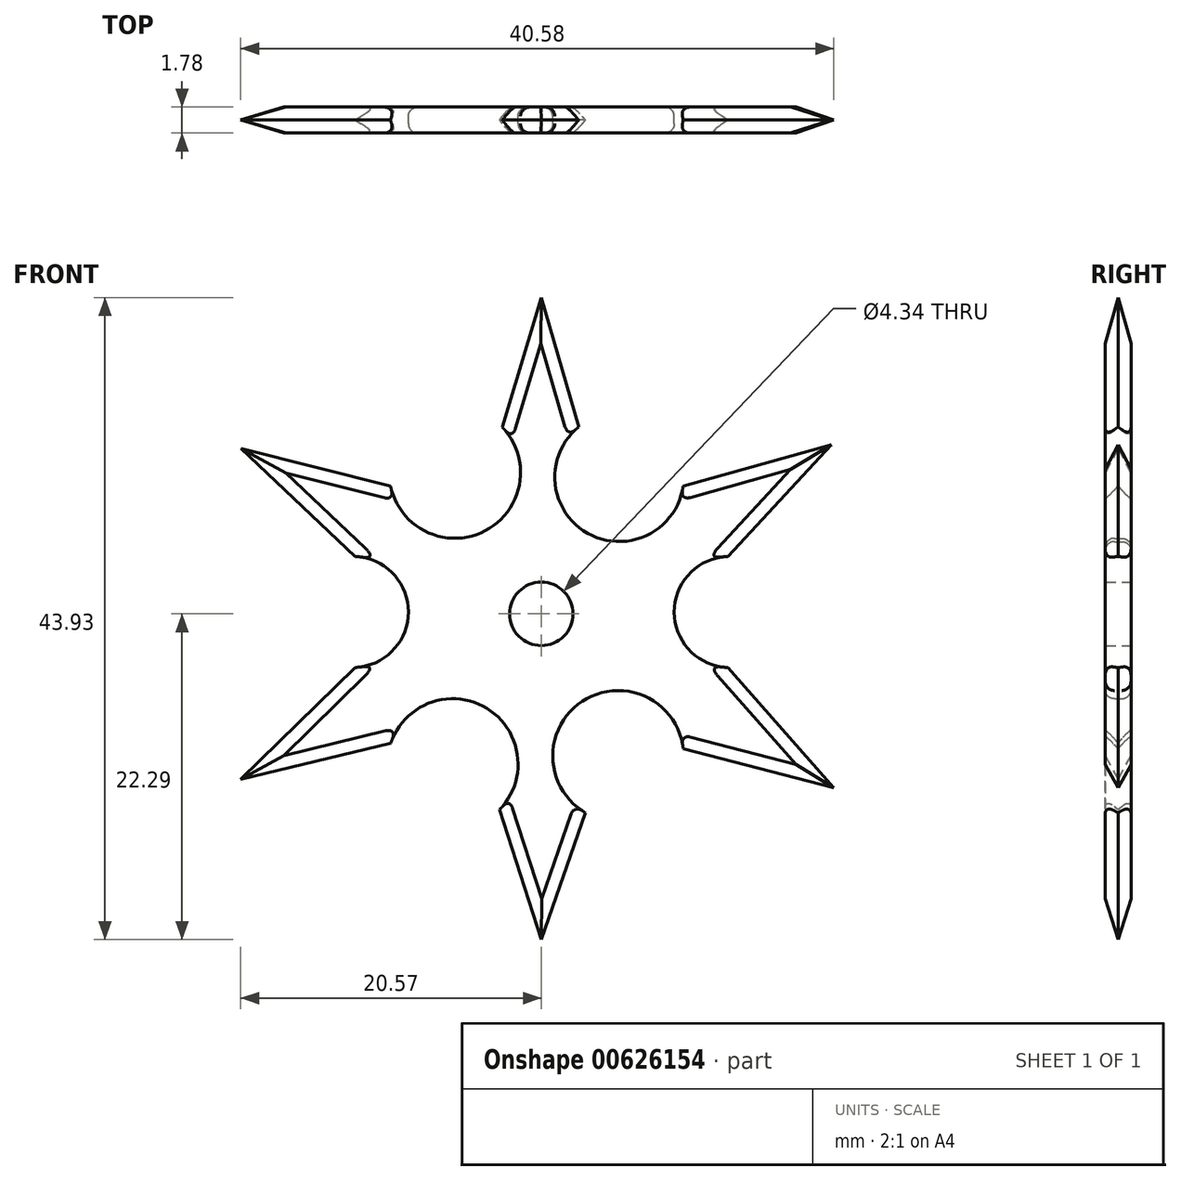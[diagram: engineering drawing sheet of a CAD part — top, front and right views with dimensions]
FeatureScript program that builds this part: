
annotation { "Feature Type Name" : "Feature", "Feature Type Description" : "" }
export const myFeature = defineFeature(function(context is Context, id is Id, definition is map)
    precondition{}
    {
        {
            var Q0;
            Q0=qCreatedBy(makeId("Front.planeOp"),FACE);
            var sketch = newSketch(context, id + "F0", { "sketchPlane" : qUnion([Q0])});
            skCircle(sketch, "E0", {"center": v(0, 0) * mm, "radius": 4.02 * mm});
            skArc(sketch, "E1", {"start": v(-12.92, -3.67) * mm, "mid": v(-9.1, 0.13) * mm, "end": v(-12.92, 3.93) * mm});
            skArc(sketch, "E2", {"start": v(12.92, 3.93) * mm, "mid": v(9.1, 0.13) * mm, "end": v(12.92, -3.67) * mm});
            skPoint(sketch, "E3.startSnap0", {"position": v(-9.1, 0.13) * mm});
            skLineSegment(sketch, "E4", {"start": v(-12.92, -3.67) * mm, "end": v(-20.98, -11.56) * mm});
            skLineSegment(sketch, "E5", {"start": v(-20.98, -11.56) * mm, "end": v(-10.34, -8.98) * mm});
            skLineSegment(sketch, "E6", {"start": v(9.72, -9.35) * mm, "end": v(20.38, -12.12) * mm});
            skLineSegment(sketch, "E7", {"start": v(12.92, -3.67) * mm, "end": v(20.38, -12.12) * mm});
            skLineSegment(sketch, "E8", {"start": v(12.92, 3.93) * mm, "end": v(20.25, 11.82) * mm});
            skLineSegment(sketch, "E9", {"start": v(9.72, 8.88) * mm, "end": v(20.25, 11.82) * mm});
            skLineSegment(sketch, "E10", {"start": v(-12.92, 3.93) * mm, "end": v(-20.98, 11.55) * mm});
            skLineSegment(sketch, "E11", {"start": v(-10.34, 8.88) * mm, "end": v(-20.98, 11.55) * mm});
            skCircle(sketch, "E12", {"center": v(0, 0) * mm, "radius": 2.17 * mm});
            skArc(sketch, "E13", {"start": v(-2.96, -13.5) * mm, "mid": v(-3.73, -6.46) * mm, "end": v(-10.34, -8.98) * mm});
            skArc(sketch, "E14", {"start": v(9.72, -9.35) * mm, "mid": v(2.8, -5.98) * mm, "end": v(3.13, -13.66) * mm});
            skLineSegment(sketch, "E15", {"start": v(-2.96, -13.5) * mm, "end": v(0, -22.69) * mm});
            skLineSegment(sketch, "E16", {"start": v(0, -22.69) * mm, "end": v(3.13, -13.66) * mm});
            skArc(sketch, "E17", {"start": v(-10.34, 8.88) * mm, "mid": v(-3.82, 5.69) * mm, "end": v(-2.77, 12.87) * mm});
            skArc(sketch, "E18", {"start": v(2.66, 12.87) * mm, "mid": v(3.16, 5.52) * mm, "end": v(9.72, 8.88) * mm});
            skLineSegment(sketch, "E19", {"start": v(-2.77, 12.87) * mm, "end": v(0, 22.1) * mm});
            skLineSegment(sketch, "E20", {"start": v(0, 22.1) * mm, "end": v(2.66, 12.87) * mm});
            skLineSegment(sketch, "E21", {"start": v(-2.77, 12.87) * mm, "end": v(2.66, 12.87) * mm});
            skLineSegment(sketch, "E22", {"start": v(-2.96, -13.5) * mm, "end": v(3.13, -13.66) * mm});
            skLineSegment(sketch, "E23", {"start": v(-12.92, -3.67) * mm, "end": v(-10.34, -8.98) * mm});
            skLineSegment(sketch, "E24", {"start": v(-12.92, 3.93) * mm, "end": v(-10.34, 8.88) * mm});
            skLineSegment(sketch, "E25", {"start": v(9.72, 8.88) * mm, "end": v(12.92, 3.93) * mm});
            skLineSegment(sketch, "E26", {"start": v(12.92, -3.67) * mm, "end": v(9.72, -9.35) * mm});
            skPoint(sketch, "E27.endSnap0", {"position": v(-11.63, 6.4) * mm});
            skLineSegment(sketch, "E28", {"start": v(-11.63, 6.4) * mm, "end": v(-20.98, 11.55) * mm});
            skLineSegment(sketch, "E29", {"start": v(0, 22.1) * mm, "end": v(0, 12.87) * mm});
            skLineSegment(sketch, "E30", {"start": v(20.25, 11.82) * mm, "end": v(11.32, 6.4) * mm});
            skLineSegment(sketch, "E31", {"start": v(20.38, -12.12) * mm, "end": v(11.32, -6.51) * mm});
            skLineSegment(sketch, "E32", {"start": v(0, -22.69) * mm, "end": v(0, -13.58) * mm});
            skLineSegment(sketch, "E33", {"start": v(-20.98, -11.56) * mm, "end": v(-11.63, -6.32) * mm});
            skLineSegment(sketch, "E34", {"start": v(-12.92, 3.93) * mm, "end": v(-16.3, 8.98) * mm});
            skLineSegment(sketch, "E35", {"start": v(-16.3, 8.98) * mm, "end": v(-10.34, 8.88) * mm});
            skLineSegment(sketch, "E36", {"start": v(-10.34, -8.98) * mm, "end": v(-16.38, -8.98) * mm});
            skLineSegment(sketch, "E37", {"start": v(-16.38, -8.98) * mm, "end": v(-12.92, -3.67) * mm});
            skLineSegment(sketch, "E38", {"start": v(-2.96, -13.5) * mm, "end": v(0, -18.8) * mm});
            skLineSegment(sketch, "E39", {"start": v(0, -18.8) * mm, "end": v(3.13, -13.66) * mm});
            skLineSegment(sketch, "E40", {"start": v(9.72, -9.35) * mm, "end": v(16.19, -9.53) * mm});
            skLineSegment(sketch, "E41", {"start": v(16.19, -9.53) * mm, "end": v(12.92, -3.67) * mm});
            skLineSegment(sketch, "E42", {"start": v(-2.77, 12.87) * mm, "end": v(0, 17.48) * mm});
            skLineSegment(sketch, "E43", {"start": v(0, 17.48) * mm, "end": v(2.66, 12.87) * mm});
            skPoint(sketch, "E44.endSnap0", {"position": v(15.78, 9.11) * mm});
            skLineSegment(sketch, "E45", {"start": v(9.72, 8.88) * mm, "end": v(15.78, 9.11) * mm});
            skLineSegment(sketch, "E46", {"start": v(15.78, 9.11) * mm, "end": v(12.92, 3.93) * mm});
            skSolve(sketch);
        }
        {
            var Q0;
            Q0=makeQuery(id+"F0.imprint","IMPRINT",FACE,{"disambiguationData":[TD([[makeQuery(id+"F0.imprint","IMPRINT",EDGE,{"derivedFrom":sQuery(id+"F0.wireOp",EDGE,"E0")}),-1.0]])]});
            var Q1;
            Q1=makeQuery(id+"F0.imprint","IMPRINT",FACE,{"disambiguationData":[TD([[makeQuery(id+"F0.imprint","IMPRINT",EDGE,{"derivedFrom":sQuery(id+"F0.wireOp",EDGE,"E0")}),1.0]])]});
            extrude(context, id + "F1", {"entities" : qUnion([Q0, Q1]), "depth" : 1.78 * mm, "symmetric" : true});
        }
        {
            var Q0;
            {var subQ0=sQuery(id+"F0.wireOp",EDGE,"E35");Q0=makeQuery(id+"F0.imprint","IMPRINT",FACE,{"disambiguationData":[TD([[makeQuery(id+"F0.imprint","IMPRINT",EDGE,{"derivedFrom":subQ0}),-1.0]])]});}
            var Q1;
            {var subQ0=sQuery(id+"F0.wireOp",EDGE,"E34");Q1=makeQuery(id+"F0.imprint","IMPRINT",FACE,{"disambiguationData":[TD([[makeQuery(id+"F0.imprint","IMPRINT",EDGE,{"derivedFrom":subQ0}),-1.0]])]});}
            var Q2;
            {var subQ0=sQuery(id+"F0.wireOp",EDGE,"E10");Q2=makeQuery(id+"F0.imprint","IMPRINT",FACE,{"disambiguationData":[TD([[makeQuery(id+"F0.imprint","IMPRINT",EDGE,{"derivedFrom":subQ0}),-1.0]])]});}
            var Q3;
            {var subQ0=sQuery(id+"F0.wireOp",EDGE,"E11");Q3=makeQuery(id+"F0.imprint","IMPRINT",FACE,{"disambiguationData":[TD([[makeQuery(id+"F0.imprint","IMPRINT",EDGE,{"derivedFrom":subQ0}),1.0]])]});}
            var Q4;
            {var subQ0=sQuery(id+"F0.wireOp",EDGE,"E42");Q4=makeQuery(id+"F0.imprint","IMPRINT",FACE,{"disambiguationData":[TD([[makeQuery(id+"F0.imprint","IMPRINT",EDGE,{"derivedFrom":subQ0}),-1.0]])]});}
            var Q5;
            {var subQ0=sQuery(id+"F0.wireOp",EDGE,"E43");Q5=makeQuery(id+"F0.imprint","IMPRINT",FACE,{"disambiguationData":[TD([[makeQuery(id+"F0.imprint","IMPRINT",EDGE,{"derivedFrom":subQ0}),-1.0]])]});}
            var Q6;
            {var subQ0=sQuery(id+"F0.wireOp",EDGE,"E20");Q6=makeQuery(id+"F0.imprint","IMPRINT",FACE,{"disambiguationData":[TD([[makeQuery(id+"F0.imprint","IMPRINT",EDGE,{"derivedFrom":subQ0}),-1.0]])]});}
            var Q7;
            {var subQ0=sQuery(id+"F0.wireOp",EDGE,"E19");Q7=makeQuery(id+"F0.imprint","IMPRINT",FACE,{"disambiguationData":[TD([[makeQuery(id+"F0.imprint","IMPRINT",EDGE,{"derivedFrom":subQ0}),-1.0]])]});}
            var Q8;
            {var subQ0=sQuery(id+"F0.wireOp",EDGE,"E5");Q8=makeQuery(id+"F0.imprint","IMPRINT",FACE,{"disambiguationData":[TD([[makeQuery(id+"F0.imprint","IMPRINT",EDGE,{"derivedFrom":subQ0}),1.0]])]});}
            var Q9;
            {var subQ0=sQuery(id+"F0.wireOp",EDGE,"E4");Q9=makeQuery(id+"F0.imprint","IMPRINT",FACE,{"disambiguationData":[TD([[makeQuery(id+"F0.imprint","IMPRINT",EDGE,{"derivedFrom":subQ0}),1.0]])]});}
            var Q10;
            {var subQ0=sQuery(id+"F0.wireOp",EDGE,"E37");Q10=makeQuery(id+"F0.imprint","IMPRINT",FACE,{"disambiguationData":[TD([[makeQuery(id+"F0.imprint","IMPRINT",EDGE,{"derivedFrom":subQ0}),-1.0]])]});}
            var Q11;
            {var subQ0=sQuery(id+"F0.wireOp",EDGE,"E36");Q11=makeQuery(id+"F0.imprint","IMPRINT",FACE,{"disambiguationData":[TD([[makeQuery(id+"F0.imprint","IMPRINT",EDGE,{"derivedFrom":subQ0}),-1.0]])]});}
            var Q12;
            {var subQ0=sQuery(id+"F0.wireOp",EDGE,"E15");Q12=makeQuery(id+"F0.imprint","IMPRINT",FACE,{"disambiguationData":[TD([[makeQuery(id+"F0.imprint","IMPRINT",EDGE,{"derivedFrom":subQ0}),1.0]])]});}
            var Q13;
            {var subQ0=sQuery(id+"F0.wireOp",EDGE,"E16");Q13=makeQuery(id+"F0.imprint","IMPRINT",FACE,{"disambiguationData":[TD([[makeQuery(id+"F0.imprint","IMPRINT",EDGE,{"derivedFrom":subQ0}),1.0]])]});}
            var Q14;
            {var subQ0=sQuery(id+"F0.wireOp",EDGE,"E39");Q14=makeQuery(id+"F0.imprint","IMPRINT",FACE,{"disambiguationData":[TD([[makeQuery(id+"F0.imprint","IMPRINT",EDGE,{"derivedFrom":subQ0}),1.0]])]});}
            var Q15;
            {var subQ0=sQuery(id+"F0.wireOp",EDGE,"E38");Q15=makeQuery(id+"F0.imprint","IMPRINT",FACE,{"disambiguationData":[TD([[makeQuery(id+"F0.imprint","IMPRINT",EDGE,{"derivedFrom":subQ0}),1.0]])]});}
            var Q16;
            {var subQ0=sQuery(id+"F0.wireOp",EDGE,"E7");Q16=makeQuery(id+"F0.imprint","IMPRINT",FACE,{"disambiguationData":[TD([[makeQuery(id+"F0.imprint","IMPRINT",EDGE,{"derivedFrom":subQ0}),-1.0]])]});}
            var Q17;
            {var subQ0=sQuery(id+"F0.wireOp",EDGE,"E41");Q17=makeQuery(id+"F0.imprint","IMPRINT",FACE,{"disambiguationData":[TD([[makeQuery(id+"F0.imprint","IMPRINT",EDGE,{"derivedFrom":subQ0}),1.0]])]});}
            var Q18;
            {var subQ0=sQuery(id+"F0.wireOp",EDGE,"E40");Q18=makeQuery(id+"F0.imprint","IMPRINT",FACE,{"disambiguationData":[TD([[makeQuery(id+"F0.imprint","IMPRINT",EDGE,{"derivedFrom":subQ0}),1.0]])]});}
            var Q19;
            {var subQ0=sQuery(id+"F0.wireOp",EDGE,"E6");Q19=makeQuery(id+"F0.imprint","IMPRINT",FACE,{"disambiguationData":[TD([[makeQuery(id+"F0.imprint","IMPRINT",EDGE,{"derivedFrom":subQ0}),1.0]])]});}
            var Q20;
            {var subQ0=sQuery(id+"F0.wireOp",EDGE,"E8");Q20=makeQuery(id+"F0.imprint","IMPRINT",FACE,{"disambiguationData":[TD([[makeQuery(id+"F0.imprint","IMPRINT",EDGE,{"derivedFrom":subQ0}),1.0]])]});}
            var Q21;
            {var subQ0=sQuery(id+"F0.wireOp",EDGE,"E9");Q21=makeQuery(id+"F0.imprint","IMPRINT",FACE,{"disambiguationData":[TD([[makeQuery(id+"F0.imprint","IMPRINT",EDGE,{"derivedFrom":subQ0}),-1.0]])]});}
            var Q22;
            {var subQ0=sQuery(id+"F0.wireOp",EDGE,"E45");Q22=makeQuery(id+"F0.imprint","IMPRINT",FACE,{"disambiguationData":[TD([[makeQuery(id+"F0.imprint","IMPRINT",EDGE,{"derivedFrom":subQ0}),-1.0]])]});}
            var Q23;
            {var subQ0=sQuery(id+"F0.wireOp",EDGE,"E46");Q23=makeQuery(id+"F0.imprint","IMPRINT",FACE,{"disambiguationData":[TD([[makeQuery(id+"F0.imprint","IMPRINT",EDGE,{"derivedFrom":subQ0}),-1.0]])]});}
            extrude(context, id + "F2", {"entities" : qUnion([Q0, Q1, Q2, Q3, Q4, Q5, Q6, Q7, Q8, Q9, Q10, Q11, Q12, Q13, Q14, Q15, Q16, Q17, Q18, Q19, Q20, Q21, Q22, Q23]), "operationType" : NewBodyOperationType.ADD, "depth" : 1.78 * mm, "symmetric" : true});
        }
        {
            var Q0;
            Q0=makeQuery(id+"F2.opExtrude","CAP_EDGE",EDGE,{"disambiguationData":[OSD([sQuery(id+"F0.wireOp",EDGE,"E11")])],"isStart":false});
            var Q1;
            Q1=makeQuery(id+"F2.opExtrude","CAP_EDGE",EDGE,{"disambiguationData":[OSD([sQuery(id+"F0.wireOp",EDGE,"E10")])],"isStart":false});
            var Q2;
            Q2=makeQuery(id+"F2.opExtrude","CAP_EDGE",EDGE,{"disambiguationData":[OSD([sQuery(id+"F0.wireOp",EDGE,"E19")])],"isStart":false});
            var Q3;
            Q3=makeQuery(id+"F2.opExtrude","CAP_EDGE",EDGE,{"disambiguationData":[OSD([sQuery(id+"F0.wireOp",EDGE,"E20")])],"isStart":false});
            var Q4;
            Q4=makeQuery(id+"F2.opExtrude","CAP_EDGE",EDGE,{"disambiguationData":[OSD([sQuery(id+"F0.wireOp",EDGE,"E9")])],"isStart":false});
            var Q5;
            Q5=makeQuery(id+"F2.opExtrude","CAP_EDGE",EDGE,{"disambiguationData":[OSD([sQuery(id+"F0.wireOp",EDGE,"E8")])],"isStart":false});
            var Q6;
            Q6=makeQuery(id+"F2.opExtrude","CAP_EDGE",EDGE,{"disambiguationData":[OSD([sQuery(id+"F0.wireOp",EDGE,"E7")])],"isStart":false});
            var Q7;
            Q7=makeQuery(id+"F2.opExtrude","CAP_EDGE",EDGE,{"disambiguationData":[OSD([sQuery(id+"F0.wireOp",EDGE,"E6")])],"isStart":false});
            var Q8;
            Q8=makeQuery(id+"F2.opExtrude","CAP_EDGE",EDGE,{"disambiguationData":[OSD([sQuery(id+"F0.wireOp",EDGE,"E16")])],"isStart":false});
            var Q9;
            Q9=makeQuery(id+"F2.opExtrude","CAP_EDGE",EDGE,{"disambiguationData":[OSD([sQuery(id+"F0.wireOp",EDGE,"E15")])],"isStart":false});
            var Q10;
            Q10=makeQuery(id+"F2.opExtrude","CAP_EDGE",EDGE,{"disambiguationData":[OSD([sQuery(id+"F0.wireOp",EDGE,"E5")])],"isStart":false});
            var Q11;
            Q11=makeQuery(id+"F2.opExtrude","CAP_EDGE",EDGE,{"disambiguationData":[OSD([sQuery(id+"F0.wireOp",EDGE,"E4")])],"isStart":false});
            chamfer(context, id + "F3", {"entities" : qUnion([Q0, Q1, Q2, Q3, Q4, Q5, Q6, Q7, Q8, Q9, Q10, Q11]), "width" : 1.02 * mm, "tangentPropagation" : true});
        }
        {
            var Q0;
            Q0=makeQuery(id+"F1.opExtrude","CAP_EDGE",EDGE,{"disambiguationData":[OSD([sQuery(id+"F0.wireOp",EDGE,"E13")])],"isStart":false});
            var Q1;
            Q1=makeQuery(id+"F1.opExtrude","CAP_EDGE",EDGE,{"disambiguationData":[OSD([sQuery(id+"F0.wireOp",EDGE,"E14")])],"isStart":false});
            var Q2;
            Q2=makeQuery(id+"F1.opExtrude","CAP_EDGE",EDGE,{"disambiguationData":[OSD([sQuery(id+"F0.wireOp",EDGE,"E2")])],"isStart":false});
            var Q3;
            Q3=makeQuery(id+"F1.opExtrude","CAP_EDGE",EDGE,{"disambiguationData":[OSD([sQuery(id+"F0.wireOp",EDGE,"E18")])],"isStart":false});
            var Q4;
            Q4=makeQuery(id+"F1.opExtrude","CAP_EDGE",EDGE,{"disambiguationData":[OSD([sQuery(id+"F0.wireOp",EDGE,"E17")])],"isStart":false});
            var Q5;
            Q5=makeQuery(id+"F1.opExtrude","CAP_EDGE",EDGE,{"disambiguationData":[OSD([sQuery(id+"F0.wireOp",EDGE,"E1")])],"isStart":false});
            fillet(context, id + "F4", {"entities" : qUnion([Q0, Q1, Q2, Q3, Q4, Q5]), "radius" : 0.64 * mm, "tangentPropagation" : true, "allowEdgeOverflow" : false});
        }
        {
            var Q0;
            Q0=makeQuery(id+"F2.opExtrude","CAP_EDGE",EDGE,{"disambiguationData":[OSD([sQuery(id+"F0.wireOp",EDGE,"E8")])],"isStart":true});
            var Q1;
            Q1=makeQuery(id+"F2.opExtrude","CAP_EDGE",EDGE,{"disambiguationData":[OSD([sQuery(id+"F0.wireOp",EDGE,"E9")])],"isStart":true});
            var Q2;
            Q2=makeQuery(id+"F2.opExtrude","CAP_EDGE",EDGE,{"disambiguationData":[OSD([sQuery(id+"F0.wireOp",EDGE,"E11")])],"isStart":true});
            var Q3;
            Q3=makeQuery(id+"F2.opExtrude","CAP_EDGE",EDGE,{"disambiguationData":[OSD([sQuery(id+"F0.wireOp",EDGE,"E10")])],"isStart":true});
            var Q4;
            Q4=makeQuery(id+"F2.opExtrude","CAP_EDGE",EDGE,{"disambiguationData":[OSD([sQuery(id+"F0.wireOp",EDGE,"E4")])],"isStart":true});
            var Q5;
            Q5=makeQuery(id+"F2.opExtrude","CAP_EDGE",EDGE,{"disambiguationData":[OSD([sQuery(id+"F0.wireOp",EDGE,"E5")])],"isStart":true});
            var Q6;
            Q6=makeQuery(id+"F2.opExtrude","CAP_EDGE",EDGE,{"disambiguationData":[OSD([sQuery(id+"F0.wireOp",EDGE,"E15")])],"isStart":true});
            var Q7;
            Q7=makeQuery(id+"F2.opExtrude","CAP_EDGE",EDGE,{"disambiguationData":[OSD([sQuery(id+"F0.wireOp",EDGE,"E16")])],"isStart":true});
            var Q8;
            Q8=makeQuery(id+"F2.opExtrude","CAP_EDGE",EDGE,{"disambiguationData":[OSD([sQuery(id+"F0.wireOp",EDGE,"E6")])],"isStart":true});
            var Q9;
            Q9=makeQuery(id+"F2.opExtrude","CAP_EDGE",EDGE,{"disambiguationData":[OSD([sQuery(id+"F0.wireOp",EDGE,"E7")])],"isStart":true});
            var Q10;
            Q10=makeQuery(id+"F2.opExtrude","CAP_EDGE",EDGE,{"disambiguationData":[OSD([sQuery(id+"F0.wireOp",EDGE,"E19")])],"isStart":true});
            var Q11;
            Q11=makeQuery(id+"F2.opExtrude","CAP_EDGE",EDGE,{"disambiguationData":[OSD([sQuery(id+"F0.wireOp",EDGE,"E20")])],"isStart":true});
            chamfer(context, id + "F5", {"entities" : qUnion([Q0, Q1, Q2, Q3, Q4, Q5, Q6, Q7, Q8, Q9, Q10, Q11]), "width" : 1.02 * mm, "tangentPropagation" : true});
        }
        {
            var Q0;
            Q0=makeQuery(id+"F1.opExtrude","CAP_EDGE",EDGE,{"disambiguationData":[OSD([sQuery(id+"F0.wireOp",EDGE,"E18")])],"isStart":true});
            var Q1;
            Q1=makeQuery(id+"F1.opExtrude","CAP_EDGE",EDGE,{"disambiguationData":[OSD([sQuery(id+"F0.wireOp",EDGE,"E17")])],"isStart":true});
            var Q2;
            Q2=makeQuery(id+"F1.opExtrude","CAP_EDGE",EDGE,{"disambiguationData":[OSD([sQuery(id+"F0.wireOp",EDGE,"E1")])],"isStart":true});
            var Q3;
            Q3=makeQuery(id+"F1.opExtrude","CAP_EDGE",EDGE,{"disambiguationData":[OSD([sQuery(id+"F0.wireOp",EDGE,"E13")])],"isStart":true});
            var Q4;
            Q4=makeQuery(id+"F1.opExtrude","CAP_EDGE",EDGE,{"disambiguationData":[OSD([sQuery(id+"F0.wireOp",EDGE,"E14")])],"isStart":true});
            var Q5;
            Q5=makeQuery(id+"F1.opExtrude","CAP_EDGE",EDGE,{"disambiguationData":[OSD([sQuery(id+"F0.wireOp",EDGE,"E2")])],"isStart":true});
            fillet(context, id + "F6", {"entities" : qUnion([Q0, Q1, Q2, Q3, Q4, Q5]), "radius" : 0.64 * mm, "tangentPropagation" : true, "allowEdgeOverflow" : false});
        }
    });
